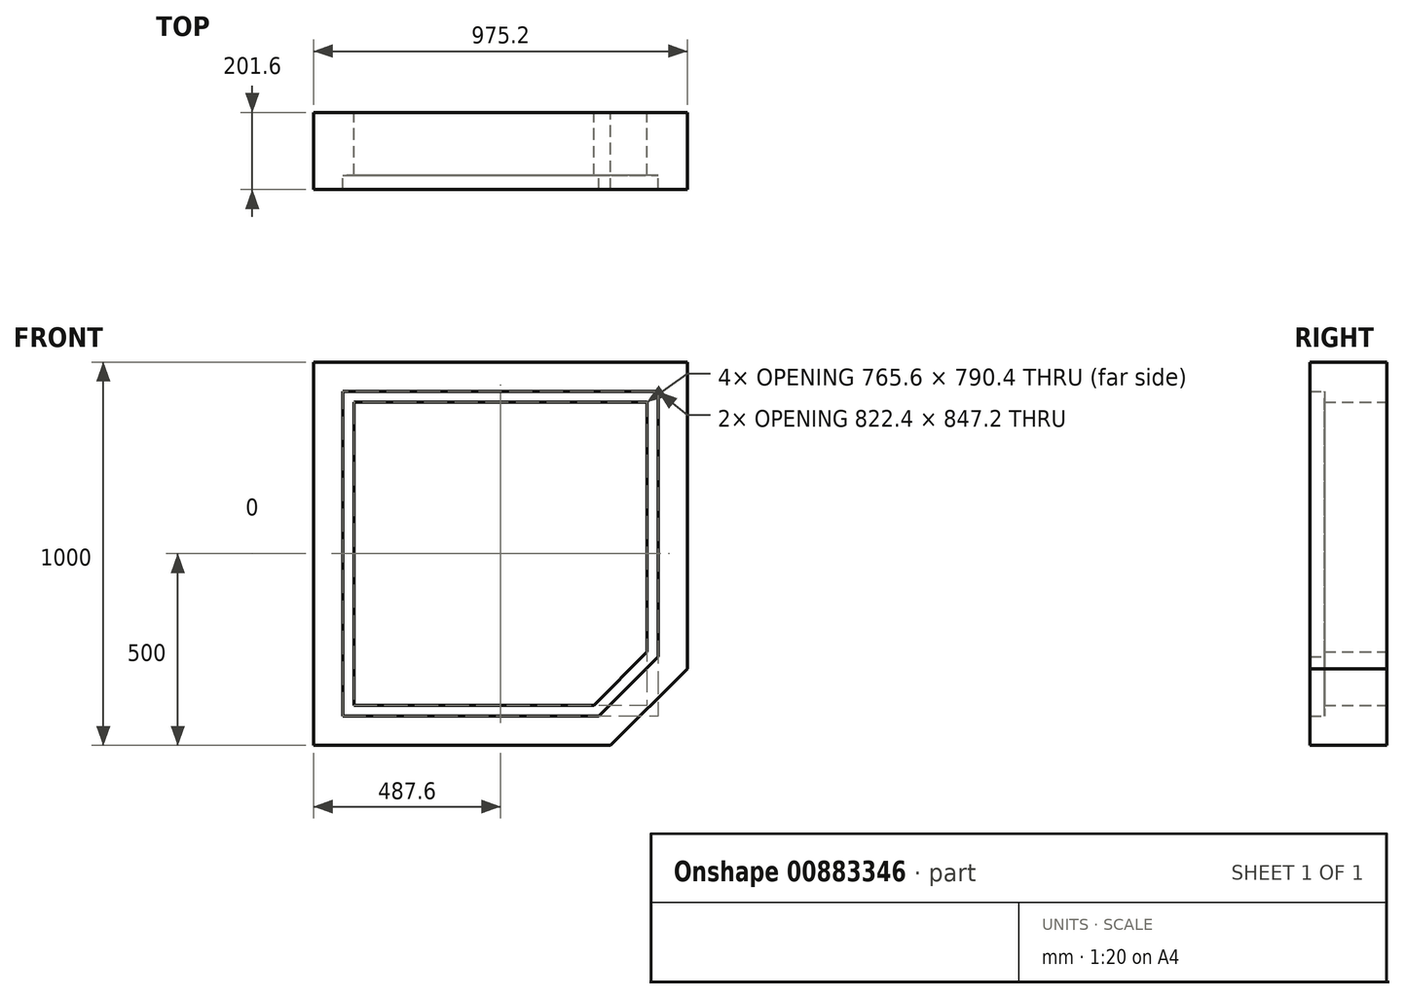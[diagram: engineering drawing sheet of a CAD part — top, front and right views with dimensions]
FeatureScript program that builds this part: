
annotation { "Feature Type Name" : "Feature", "Feature Type Description" : "" }
export const myFeature = defineFeature(function(context is Context, id is Id, definition is map)
    precondition{}
    {
        {
            var Q0;
            Q0=qCreatedBy(makeId("Right.planeOp"),FACE);
            var sketch = newSketch(context, id + "F0", { "sketchPlane" : qUnion([Q0])});
            skLineSegment(sketch, "E0", {"start": v(-201.6, 76.4) * mm, "end": v(-163.6, 76.4) * mm});
            skLineSegment(sketch, "E1", {"start": v(-163.6, 76.4) * mm, "end": v(-163.6, 104.8) * mm});
            skLineSegment(sketch, "E2", {"start": v(-201.6, 76.4) * mm, "end": v(-201.6, 0) * mm});
            skLineSegment(sketch, "E3", {"start": v(-201.6, 0) * mm, "end": v(0, 0) * mm});
            skLineSegment(sketch, "E4", {"start": v(0, 0) * mm, "end": v(0, 104.8) * mm});
            skLineSegment(sketch, "E5", {"start": v(0, 104.8) * mm, "end": v(-163.6, 104.8) * mm});
            skSolve(sketch);
        }
        {
            var Q0;
            Q0=qCreatedBy(makeId("Front.planeOp"),FACE);
            var sketch = newSketch(context, id + "F1", { "sketchPlane" : qUnion([Q0])});
            skLineSegment(sketch, "E6", {"start": v(0, 0) * mm, "end": v(287.6, 0) * mm});
            skLineSegment(sketch, "E7", {"start": v(487.6, 200) * mm, "end": v(487.6, 1000) * mm});
            skLineSegment(sketch, "E8", {"start": v(487.6, 1000) * mm, "end": v(-487.6, 1000) * mm});
            skLineSegment(sketch, "E9", {"start": v(-487.6, 1000) * mm, "end": v(-487.6, 0) * mm});
            skLineSegment(sketch, "E10", {"start": v(-487.6, 0) * mm, "end": v(0, 0) * mm});
            skLineSegment(sketch, "E11", {"start": v(287.6, 0) * mm, "end": v(487.6, 200) * mm});
            skPoint(sketch, "E12.orphan", {"position": v(487.6, 0) * mm});
            skSolve(sketch);
        }
        {
            var Q0;
            Q0=makeQuery(id+"F0.imprint","IMPRINT",FACE,{"disambiguationData":[TD([[makeQuery(id+"F0.imprint","IMPRINT",EDGE,{"derivedFrom":sQuery(id+"F0.wireOp",EDGE,"E0")}),-1.0]])]});
            var Q1;
            Q1=sQuery(id+"F1.wireOp",EDGE,"E6");
            var Q2;
            Q2=sQuery(id+"F1.wireOp",EDGE,"E11");
            var Q3;
            Q3=sQuery(id+"F1.wireOp",EDGE,"E7");
            var Q4;
            Q4=sQuery(id+"F1.wireOp",EDGE,"E8");
            var Q5;
            Q5=sQuery(id+"F1.wireOp",EDGE,"E9");
            var Q6;
            Q6=sQuery(id+"F1.wireOp",EDGE,"E10");
            sweep(context, id + "F2", {"profiles" : qUnion([Q0]), "path" : qUnion([Q1, Q2, Q3, Q4, Q5, Q6])});
        }
    });
